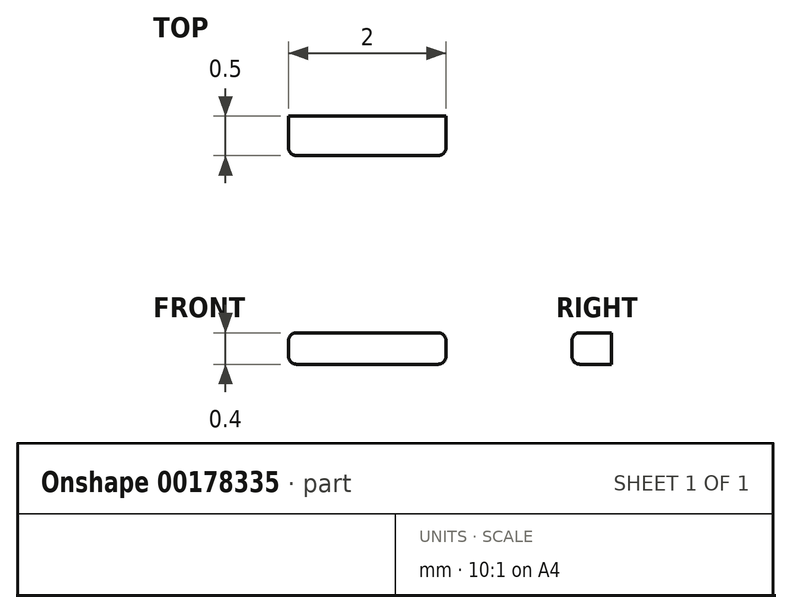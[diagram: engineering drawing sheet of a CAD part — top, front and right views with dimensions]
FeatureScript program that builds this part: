
annotation { "Feature Type Name" : "Feature", "Feature Type Description" : "" }
export const myFeature = defineFeature(function(context is Context, id is Id, definition is map)
    precondition{}
    {
        {
            var Q0;
            Q0=qCreatedBy(makeId("Front.planeOp"),FACE);
            var sketch = newSketch(context, id + "F0", { "sketchPlane" : qUnion([Q0])});
            skLineSegment(sketch, "E0.bottom", {"start": v(1, 0.2) * mm, "end": v(-1, 0.2) * mm});
            skLineSegment(sketch, "E0.top", {"start": v(1, -0.2) * mm, "end": v(-1, -0.2) * mm});
            skLineSegment(sketch, "E0.left", {"start": v(1, 0.2) * mm, "end": v(1, -0.2) * mm});
            skLineSegment(sketch, "E0.right", {"start": v(-1, 0.2) * mm, "end": v(-1, -0.2) * mm});
            skPoint(sketch, "E0.middle", {"position": v(0, 0) * mm});
            skSolve(sketch);
        }
        {
            var Q0;
            Q0 = qSketchRegion(id + "F0", true);
            extrude(context, id + "F1", {"entities" : qUnion([Q0]), "depth" : 0.5 * mm});
        }
        {
            var Q0;
            Q0=makeQuery(id+"F1.opExtrude","CAP_EDGE",EDGE,{"disambiguationData":[OSD([sQuery(id+"F0.wireOp",EDGE,"E0.bottom")])],"isStart":false});
            var Q1;
            Q1=makeQuery(id+"F1.opExtrude","SWEPT_EDGE",EDGE,{"disambiguationData":[OSD([sQuery(id+"F0.wireOp",EDGE,"E0.bottom"),sQuery(id+"F0.wireOp",EDGE,"E0.left")])]});
            var Q2;
            Q2=makeQuery(id+"F1.opExtrude","CAP_EDGE",EDGE,{"disambiguationData":[OSD([sQuery(id+"F0.wireOp",EDGE,"E0.left")])],"isStart":false});
            var Q3;
            Q3=makeQuery(id+"F1.opExtrude","CAP_EDGE",EDGE,{"disambiguationData":[OSD([sQuery(id+"F0.wireOp",EDGE,"E0.right")])],"isStart":false});
            var Q4;
            Q4=makeQuery(id+"F1.opExtrude","SWEPT_EDGE",EDGE,{"disambiguationData":[OSD([sQuery(id+"F0.wireOp",EDGE,"E0.top"),sQuery(id+"F0.wireOp",EDGE,"E0.right")])]});
            var Q5;
            Q5=makeQuery(id+"F1.opExtrude","CAP_EDGE",EDGE,{"disambiguationData":[OSD([sQuery(id+"F0.wireOp",EDGE,"E0.top")])],"isStart":false});
            var Q6;
            Q6=makeQuery(id+"F1.opExtrude","SWEPT_EDGE",EDGE,{"disambiguationData":[OSD([sQuery(id+"F0.wireOp",EDGE,"E0.top"),sQuery(id+"F0.wireOp",EDGE,"E0.left")])]});
            var Q7;
            Q7=makeQuery(id+"F1.opExtrude","SWEPT_EDGE",EDGE,{"disambiguationData":[OSD([sQuery(id+"F0.wireOp",EDGE,"E0.bottom"),sQuery(id+"F0.wireOp",EDGE,"E0.right")])]});
            fillet(context, id + "F2", {"entities" : qUnion([Q0, Q1, Q2, Q3, Q4, Q5, Q6, Q7]), "radius" : 0.1 * mm, "tangentPropagation" : true, "allowEdgeOverflow" : false});
        }
    });
